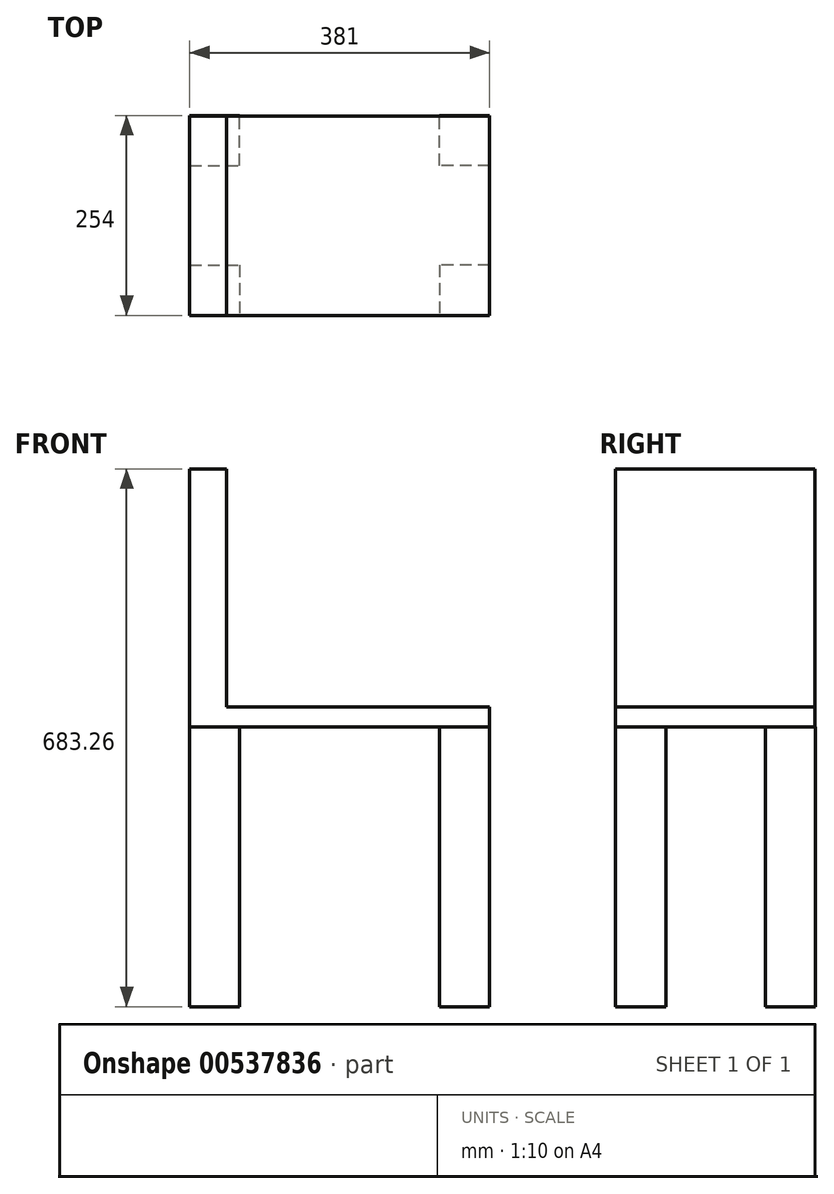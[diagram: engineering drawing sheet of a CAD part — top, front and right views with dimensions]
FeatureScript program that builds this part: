
annotation { "Feature Type Name" : "Feature", "Feature Type Description" : "" }
export const myFeature = defineFeature(function(context is Context, id is Id, definition is map)
    precondition{}
    {
        {
            var Q0;
            Q0=qCreatedBy(makeId("Top.planeOp"),FACE);
            var sketch = newSketch(context, id + "F0", { "sketchPlane" : qUnion([Q0])});
            skLineSegment(sketch, "E0", {"start": v(0, 63.77) * mm, "end": v(63.5, 63.77) * mm});
            skLineSegment(sketch, "E1", {"start": v(63.5, 63.77) * mm, "end": v(63.5, 0) * mm});
            skLineSegment(sketch, "E2", {"start": v(63.5, 0) * mm, "end": v(0, 0) * mm});
            skLineSegment(sketch, "E3", {"start": v(0, 0) * mm, "end": v(0, 63.77) * mm});
            skLineSegment(sketch, "E4", {"start": v(63.5, 0) * mm, "end": v(317.5, 0) * mm});
            skLineSegment(sketch, "E5", {"start": v(190.5, 0) * mm, "end": v(190.5, 254) * mm});
            skLineSegment(sketch, "E6.MirrorCS", {"start": v(381, 63.77) * mm, "end": v(317.5, 63.77) * mm});
            skLineSegment(sketch, "E7.MirrorCS", {"start": v(381, 0) * mm, "end": v(381, 63.77) * mm});
            skLineSegment(sketch, "E8.MirrorCS", {"start": v(317.5, 0) * mm, "end": v(381, 0) * mm});
            skLineSegment(sketch, "E9.MirrorCS", {"start": v(317.5, 63.77) * mm, "end": v(317.5, 0) * mm});
            skLineSegment(sketch, "E10", {"start": v(190.5, 127) * mm, "end": v(50.2, 127) * mm});
            skPoint(sketch, "E10.endSnap0", {"position": v(190.5, 127) * mm});
            skLineSegment(sketch, "E11.MirrorCS", {"start": v(0, 190.23) * mm, "end": v(63.5, 190.23) * mm});
            skLineSegment(sketch, "E12.MirrorCS", {"start": v(0, 254) * mm, "end": v(0, 190.23) * mm});
            skLineSegment(sketch, "E13.MirrorCS", {"start": v(63.5, 190.23) * mm, "end": v(63.5, 254) * mm});
            skLineSegment(sketch, "E14.MirrorCS", {"start": v(63.5, 254) * mm, "end": v(0, 254) * mm});
            skLineSegment(sketch, "E15.MirrorCS", {"start": v(381, 190.23) * mm, "end": v(317.5, 190.23) * mm});
            skLineSegment(sketch, "E16.MirrorCS", {"start": v(317.5, 190.23) * mm, "end": v(317.5, 254) * mm});
            skLineSegment(sketch, "E17.MirrorCS", {"start": v(317.5, 254) * mm, "end": v(381, 254) * mm});
            skLineSegment(sketch, "E18.MirrorCS", {"start": v(381, 254) * mm, "end": v(381, 190.23) * mm});
            skSolve(sketch);
        }
        {
            var Q0;
            Q0 = qSketchRegion(id + "F0", true);
            extrude(context, id + "F1", {"entities" : qUnion([Q0]), "depth" : 355.6 * mm, "offsetDistance" : 25.4 * mm});
        }
        {
            var Q0;
            Q0=makeQuery(id+"F1.opExtrude","CAP_FACE",FACE,{"disambiguationData":[OSD([sQuery(id+"F0.wireOp",EDGE,"E6.MirrorCS"),sQuery(id+"F0.wireOp",EDGE,"E7.MirrorCS"),sQuery(id+"F0.wireOp",EDGE,"E8.MirrorCS"),sQuery(id+"F0.wireOp",EDGE,"E9.MirrorCS")])],"isStart":false});
            var sketch = newSketch(context, id + "F2", { "sketchPlane" : qUnion([Q0])});
            skLineSegment(sketch, "E19", {"start": v(381, 0) * mm, "end": v(0, 0) * mm});
            skLineSegment(sketch, "E20", {"start": v(0, 0) * mm, "end": v(0, 252.96) * mm});
            skLineSegment(sketch, "E21", {"start": v(0, 252.96) * mm, "end": v(381, 252.96) * mm});
            skLineSegment(sketch, "E22", {"start": v(381, 252.96) * mm, "end": v(381, 0) * mm});
            skSolve(sketch);
        }
        {
            var Q0;
            Q0 = qSketchRegion(id + "F2", true);
            extrude(context, id + "F3", {"entities" : qUnion([Q0]), "depth" : 25.4 * mm, "offsetDistance" : 25.4 * mm});
        }
        {
            var Q0;
            Q0=makeQuery(id+"F3.opExtrude","CAP_FACE",FACE,{"disambiguationData":[OSD([sQuery(id+"F2.wireOp",EDGE,"E19"),sQuery(id+"F2.wireOp",EDGE,"E20"),sQuery(id+"F2.wireOp",EDGE,"E21"),sQuery(id+"F2.wireOp",EDGE,"E22")])],"isStart":false});
            var sketch = newSketch(context, id + "F4", { "sketchPlane" : qUnion([Q0])});
            skLineSegment(sketch, "E23", {"start": v(0, 252.96) * mm, "end": v(0, 0) * mm});
            skLineSegment(sketch, "E24", {"start": v(0, 0) * mm, "end": v(46.74, 0) * mm});
            skLineSegment(sketch, "E25", {"start": v(46.74, 0) * mm, "end": v(46.74, 252.96) * mm});
            skLineSegment(sketch, "E26", {"start": v(46.74, 252.96) * mm, "end": v(0, 252.96) * mm});
            skSolve(sketch);
        }
        {
            var Q0;
            Q0 = qSketchRegion(id + "F4", true);
            extrude(context, id + "F5", {"entities" : qUnion([Q0]), "operationType" : NewBodyOperationType.ADD, "depth" : 302.26 * mm, "offsetDistance" : 25.4 * mm});
        }
    });
